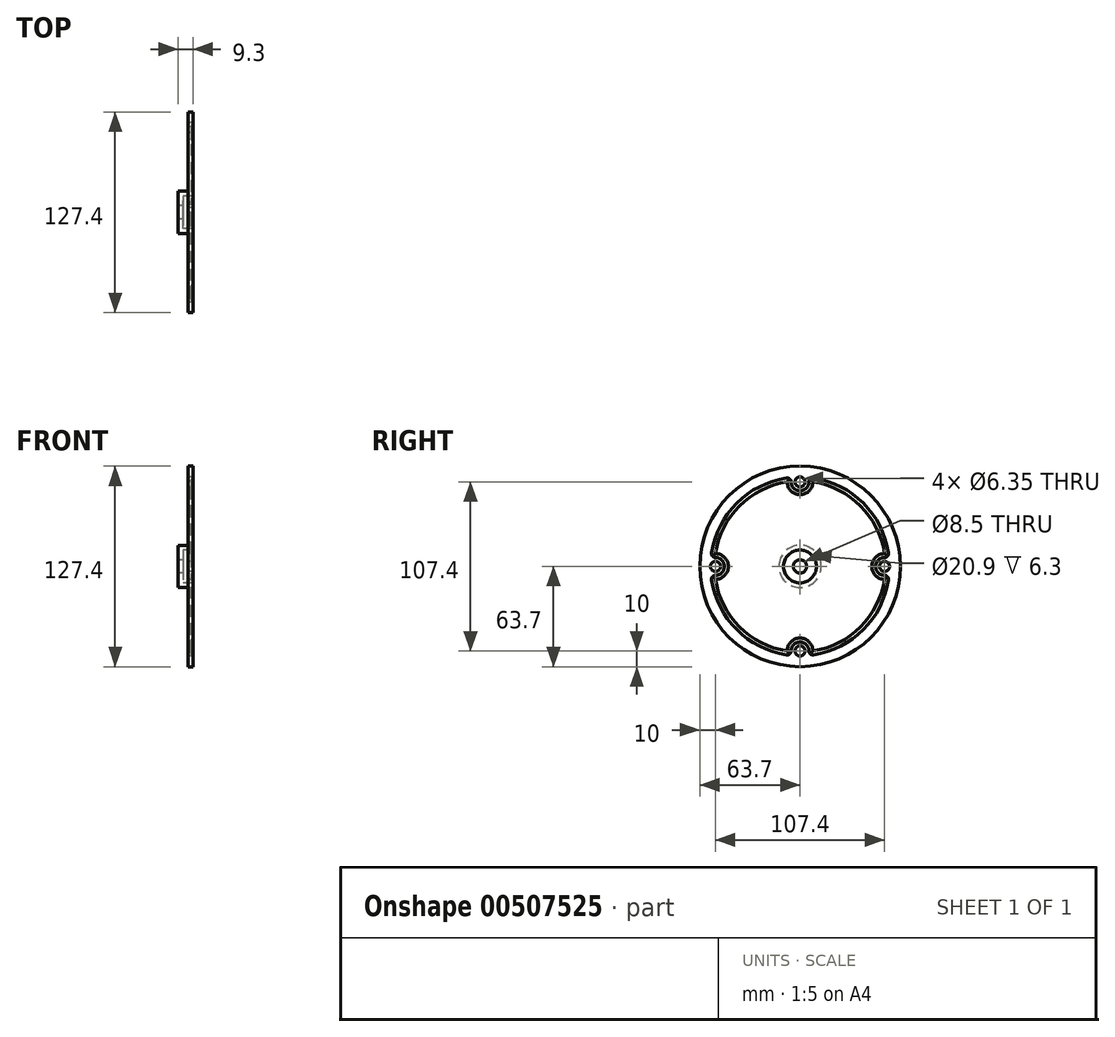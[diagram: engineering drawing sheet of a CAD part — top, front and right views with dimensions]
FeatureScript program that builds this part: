
annotation { "Feature Type Name" : "Feature", "Feature Type Description" : "" }
export const myFeature = defineFeature(function(context is Context, id is Id, definition is map)
    precondition{}
    {
        {
            var Q0;
            Q0=qCreatedBy(makeId("Top.planeOp"),FACE);
            var sketch = newSketch(context, id + "F0", { "sketchPlane" : qUnion([Q0])});
            skLineSegment(sketch, "E0", {"start": v(0, 4.25) * mm, "end": v(3, 4.25) * mm});
            skLineSegment(sketch, "E1", {"start": v(3, 4.25) * mm, "end": v(3, 10.45) * mm});
            skLineSegment(sketch, "E2", {"start": v(3, 10.45) * mm, "end": v(9.3, 10.45) * mm});
            skLineSegment(sketch, "E3", {"start": v(9.3, 10.45) * mm, "end": v(9.3, 63.7) * mm});
            skLineSegment(sketch, "E4", {"start": v(9.3, 63.7) * mm, "end": v(6.3, 63.7) * mm});
            skLineSegment(sketch, "E5", {"start": v(6.3, 63.7) * mm, "end": v(6.3, 13.45) * mm});
            skLineSegment(sketch, "E6", {"start": v(6.3, 13.45) * mm, "end": v(0, 13.45) * mm});
            skLineSegment(sketch, "E7", {"start": v(0, 13.45) * mm, "end": v(0, 4.25) * mm});
            skLineSegment(sketch, "E8", {"start": v(6.3, 43.7) * mm, "end": v(9.3, 43.7) * mm, "construction": true});
            skLineSegment(sketch, "E9", {"start": v(6.3, 63.7) * mm, "end": v(6.3, 43.7) * mm});
            skPoint(sketch, "E10", {"position": v(6.3, 53.7) * mm});
            skSolve(sketch);
        }
        {
            var Q0;
            Q0=qCreatedBy(makeId("Top.planeOp"),FACE);
            var sketch = newSketch(context, id + "F1", { "sketchPlane" : qUnion([Q0])});
            skLineSegment(sketch, "E11", {"start": v(-34.57, 0) * mm, "end": v(36.86, 0) * mm});
            skSolve(sketch);
        }
        {
            var Q0;
            Q0=makeQuery(id+"F0.imprint","IMPRINT",FACE,{"disambiguationData":[TD([[makeQuery(id+"F0.imprint","IMPRINT",EDGE,{"derivedFrom":sQuery(id+"F0.wireOp",EDGE,"E0")}),1.0]])]});
            var Q1;
            Q1=sQuery(id+"F1.wireOp",EDGE,"E11");
            revolve(context, id + "F2", {"entities" : qUnion([Q0]), "axis" : qUnion([Q1]), "revolveType" : RevolveType.FULL});
        }
        {
            var Q0;
            Q0=makeQuery(id+"F2.opRevolve","SWEPT_FACE",FACE,{"disambiguationData":[OSD([sQuery(id+"F0.wireOp",EDGE,"E5"),sQuery(id+"F0.wireOp",EDGE,"E9")])]});
            var sketch = newSketch(context, id + "F3", { "sketchPlane" : qUnion([Q0])});
            skPoint(sketch, "E12", {"position": v(-53.7, 0) * mm});
            skCircle(sketch, "E13", {"center": v(-53.7, 0) * mm, "radius": 3.17 * mm});
            skCircle(sketch, "E14.1.0", {"center": v(0, -53.7) * mm, "radius": 3.17 * mm});
            skCircle(sketch, "E14.2.0", {"center": v(53.7, 0) * mm, "radius": 3.17 * mm});
            skCircle(sketch, "E14.3.0", {"center": v(0, 53.7) * mm, "radius": 3.17 * mm});
            skPoint(sketch, "E14.center", {"position": v(0, 0) * mm});
            skSolve(sketch);
        }
        {
            var Q0;
            Q0=qSketchRegion(id+"F3",true);
            extrude(context, id + "F4", {"entities" : qUnion([Q0]), "operationType" : NewBodyOperationType.REMOVE, "oppositeDirection" : true, "depth" : 25 * mm});
        }
        {
            var Q0;
            Q0=makeQuery(id+"F2.opRevolve","SWEPT_FACE",FACE,{"disambiguationData":[OSD([sQuery(id+"F0.wireOp",EDGE,"E3")])]});
            var sketch = newSketch(context, id + "F5", { "sketchPlane" : qUnion([Q0])});
            skCircle(sketch, "E15.0", {"center": v(-53.7, 0) * mm, "radius": 3.17 * mm});
            skCircle(sketch, "E16.0", {"center": v(0, 53.7) * mm, "radius": 3.17 * mm});
            skCircle(sketch, "E17.0", {"center": v(53.7, 0) * mm, "radius": 3.17 * mm});
            skCircle(sketch, "E18.0", {"center": v(0, -53.7) * mm, "radius": 3.17 * mm});
            skPoint(sketch, "E19.center", {"position": v(0, 0) * mm});
            skArc(sketch, "E20", {"start": v(-8.17, 53.7) * mm, "mid": v(-38.4, 38.4) * mm, "end": v(-53.7, 8.17) * mm});
            skArc(sketch, "E21", {"start": v(-53.7, -8.18) * mm, "mid": v(-45.52, 0) * mm, "end": v(-53.7, 8.17) * mm});
            skArc(sketch, "E22.1.0", {"start": v(-53.7, -8.17) * mm, "mid": v(-38.4, -38.4) * mm, "end": v(-8.17, -53.7) * mm});
            skArc(sketch, "E22.1.1", {"start": v(8.18, -53.7) * mm, "mid": v(0, -45.52) * mm, "end": v(-8.17, -53.7) * mm});
            skArc(sketch, "E22.2.0", {"start": v(8.17, -53.7) * mm, "mid": v(38.4, -38.4) * mm, "end": v(53.7, -8.17) * mm});
            skArc(sketch, "E22.2.1", {"start": v(53.7, 8.18) * mm, "mid": v(45.52, 0) * mm, "end": v(53.7, -8.17) * mm});
            skArc(sketch, "E22.3.0", {"start": v(53.7, 8.17) * mm, "mid": v(38.4, 38.4) * mm, "end": v(8.17, 53.7) * mm});
            skArc(sketch, "E22.3.1", {"start": v(-8.17, 53.7) * mm, "mid": v(0, 45.52) * mm, "end": v(8.17, 53.7) * mm});
            skArc(sketch, "E23.0.startCap", {"start": v(56.17, 8.55) * mm, "mid": v(54.08, 5.7) * mm, "end": v(51.23, 7.8) * mm});
            skArc(sketch, "E23.0.endCap", {"start": v(7.8, 51.23) * mm, "mid": v(5.7, 54.08) * mm, "end": v(8.55, 56.17) * mm});
            skArc(sketch, "E23.0.left", {"start": v(51.23, 7.8) * mm, "mid": v(36.64, 36.64) * mm, "end": v(7.8, 51.23) * mm});
            skArc(sketch, "E23.0.right", {"start": v(56.17, 8.55) * mm, "mid": v(40.18, 40.18) * mm, "end": v(8.55, 56.17) * mm});
            skArc(sketch, "E23.1.startCap", {"start": v(-10.67, 53.7) * mm, "mid": v(-8.17, 56.2) * mm, "end": v(-5.67, 53.7) * mm});
            skArc(sketch, "E23.1.endCap", {"start": v(5.67, 53.7) * mm, "mid": v(8.17, 56.2) * mm, "end": v(10.67, 53.7) * mm});
            skArc(sketch, "E23.1.left", {"start": v(-5.67, 53.7) * mm, "mid": v(0, 48.02) * mm, "end": v(5.67, 53.7) * mm});
            skArc(sketch, "E23.1.right", {"start": v(-10.67, 53.7) * mm, "mid": v(0, 43.02) * mm, "end": v(10.67, 53.7) * mm});
            skArc(sketch, "E23.2.startCap", {"start": v(-8.55, 56.17) * mm, "mid": v(-5.7, 54.08) * mm, "end": v(-7.8, 51.23) * mm});
            skArc(sketch, "E23.2.endCap", {"start": v(-51.23, 7.8) * mm, "mid": v(-54.08, 5.7) * mm, "end": v(-56.17, 8.55) * mm});
            skArc(sketch, "E23.2.left", {"start": v(-7.8, 51.23) * mm, "mid": v(-36.64, 36.64) * mm, "end": v(-51.23, 7.8) * mm});
            skArc(sketch, "E23.2.right", {"start": v(-8.55, 56.17) * mm, "mid": v(-40.18, 40.18) * mm, "end": v(-56.17, 8.55) * mm});
            skArc(sketch, "E23.3.startCap", {"start": v(-53.7, -10.68) * mm, "mid": v(-56.2, -8.18) * mm, "end": v(-53.7, -5.68) * mm});
            skArc(sketch, "E23.3.endCap", {"start": v(-53.7, 5.67) * mm, "mid": v(-56.2, 8.17) * mm, "end": v(-53.7, 10.67) * mm});
            skArc(sketch, "E23.3.left", {"start": v(-53.7, -5.68) * mm, "mid": v(-48.02, 0) * mm, "end": v(-53.7, 5.67) * mm});
            skArc(sketch, "E23.3.right", {"start": v(-53.7, -10.68) * mm, "mid": v(-43.02, 0) * mm, "end": v(-53.7, 10.67) * mm});
            skArc(sketch, "E23.4.startCap", {"start": v(-56.17, -8.55) * mm, "mid": v(-54.08, -5.7) * mm, "end": v(-51.23, -7.8) * mm});
            skArc(sketch, "E23.4.endCap", {"start": v(-7.8, -51.23) * mm, "mid": v(-5.7, -54.08) * mm, "end": v(-8.55, -56.17) * mm});
            skArc(sketch, "E23.4.left", {"start": v(-51.23, -7.8) * mm, "mid": v(-36.64, -36.64) * mm, "end": v(-7.8, -51.23) * mm});
            skArc(sketch, "E23.4.right", {"start": v(-56.17, -8.55) * mm, "mid": v(-40.18, -40.18) * mm, "end": v(-8.55, -56.17) * mm});
            skArc(sketch, "E23.5.startCap", {"start": v(10.68, -53.7) * mm, "mid": v(8.18, -56.2) * mm, "end": v(5.68, -53.7) * mm});
            skArc(sketch, "E23.5.endCap", {"start": v(-5.67, -53.7) * mm, "mid": v(-8.17, -56.2) * mm, "end": v(-10.67, -53.7) * mm});
            skArc(sketch, "E23.5.left", {"start": v(5.67, -53.7) * mm, "mid": v(0, -48.02) * mm, "end": v(-5.67, -53.7) * mm});
            skArc(sketch, "E23.5.right", {"start": v(10.68, -53.7) * mm, "mid": v(0, -43.02) * mm, "end": v(-10.67, -53.7) * mm});
            skArc(sketch, "E23.6.startCap", {"start": v(8.55, -56.17) * mm, "mid": v(5.7, -54.08) * mm, "end": v(7.8, -51.23) * mm});
            skArc(sketch, "E23.6.endCap", {"start": v(51.23, -7.8) * mm, "mid": v(54.08, -5.7) * mm, "end": v(56.17, -8.55) * mm});
            skArc(sketch, "E23.6.left", {"start": v(7.8, -51.23) * mm, "mid": v(36.64, -36.64) * mm, "end": v(51.23, -7.8) * mm});
            skArc(sketch, "E23.6.right", {"start": v(8.55, -56.17) * mm, "mid": v(40.18, -40.18) * mm, "end": v(56.17, -8.55) * mm});
            skArc(sketch, "E23.7.startCap", {"start": v(53.7, 10.68) * mm, "mid": v(56.2, 8.18) * mm, "end": v(53.7, 5.68) * mm});
            skArc(sketch, "E23.7.endCap", {"start": v(53.7, -5.67) * mm, "mid": v(56.2, -8.17) * mm, "end": v(53.7, -10.67) * mm});
            skArc(sketch, "E23.7.left", {"start": v(53.7, 5.67) * mm, "mid": v(48.02, 0) * mm, "end": v(53.7, -5.67) * mm});
            skArc(sketch, "E23.7.right", {"start": v(53.7, 10.68) * mm, "mid": v(43.02, 0) * mm, "end": v(53.7, -10.67) * mm});
            skSolve(sketch);
        }
        {
            var Q0;
            Q0=qSketchRegion(id+"F5",true);
            extrude(context, id + "F6", {"entities" : qUnion([Q0]), "operationType" : NewBodyOperationType.REMOVE, "oppositeDirection" : true, "depth" : 1 * mm});
        }
        {
            var Q0;
            Q0=makeQuery(id+"F6.boolean.opBoolean","COPY",FACE,{"derivedFrom":makeQuery(id+"F6.opExtrude","CAP_FACE",FACE,{"disambiguationData":[OSD([sQuery(id+"F5.wireOp",EDGE,"E20"),sQuery(id+"F5.wireOp",EDGE,"E21"),sQuery(id+"F5.wireOp",EDGE,"E22.1.0"),sQuery(id+"F5.wireOp",EDGE,"E22.1.1"),sQuery(id+"F5.wireOp",EDGE,"E22.2.0"),sQuery(id+"F5.wireOp",EDGE,"E22.2.1"),sQuery(id+"F5.wireOp",EDGE,"E22.3.0"),sQuery(id+"F5.wireOp",EDGE,"E22.3.1"),sQuery(id+"F5.wireOp",EDGE,"E23.0.right"),sQuery(id+"F5.wireOp",EDGE,"E23.1.endCap"),sQuery(id+"F5.wireOp",EDGE,"E23.1.left"),sQuery(id+"F5.wireOp",EDGE,"E23.2.startCap"),sQuery(id+"F5.wireOp",EDGE,"E23.2.right"),sQuery(id+"F5.wireOp",EDGE,"E23.3.endCap"),sQuery(id+"F5.wireOp",EDGE,"E23.3.left"),sQuery(id+"F5.wireOp",EDGE,"E23.4.startCap"),sQuery(id+"F5.wireOp",EDGE,"E23.4.right"),sQuery(id+"F5.wireOp",EDGE,"E23.5.endCap"),sQuery(id+"F5.wireOp",EDGE,"E23.5.left"),sQuery(id+"F5.wireOp",EDGE,"E23.6.startCap"),sQuery(id+"F5.wireOp",EDGE,"E23.6.right"),sQuery(id+"F5.wireOp",EDGE,"E23.7.startCap"),sQuery(id+"F5.wireOp",EDGE,"E23.7.endCap"),sQuery(id+"F5.wireOp",EDGE,"E23.7.left")])],"isStart":false})});
            fillet(context, id + "F7", {"entities" : qUnion([Q0]), "radius" : 1.25 * mm, "tangentPropagation" : true, "allowEdgeOverflow" : false});
        }
    });
